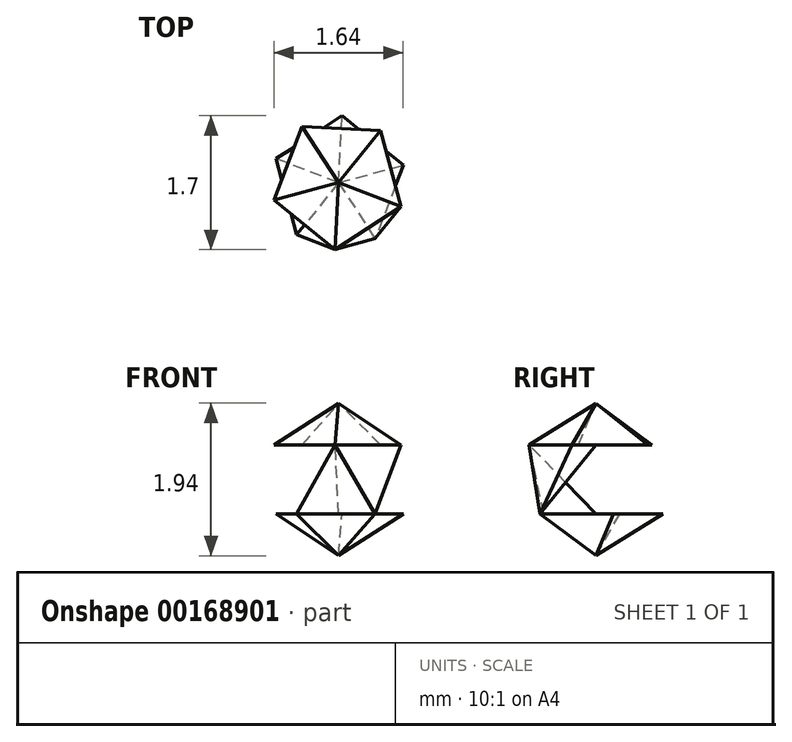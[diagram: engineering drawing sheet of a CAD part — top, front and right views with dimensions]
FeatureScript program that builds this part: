
annotation { "Feature Type Name" : "Feature", "Feature Type Description" : "" }
export const myFeature = defineFeature(function(context is Context, id is Id, definition is map)
    precondition{}
    {
        {
            var Q0;
            Q0=qCreatedBy(makeId("Top.planeOp"),FACE);
            var sketch = newSketch(context, id + "F0", { "sketchPlane" : qUnion([Q0])});
            skCircle(sketch, "E0.cCircle", {"center": v(0, 0) * mm, "radius": 0.69 * mm, "construction": true});
            skLineSegment(sketch, "E0.0", {"start": v(-0.04, -0.85) * mm, "end": v(-0.82, -0.22) * mm});
            skLineSegment(sketch, "E0.1", {"start": v(-0.82, -0.22) * mm, "end": v(-0.46, 0.71) * mm});
            skLineSegment(sketch, "E0.2", {"start": v(-0.46, 0.71) * mm, "end": v(0.53, 0.66) * mm});
            skLineSegment(sketch, "E0.3", {"start": v(0.53, 0.66) * mm, "end": v(0.8, -0.3) * mm});
            skLineSegment(sketch, "E0.4", {"start": v(0.8, -0.3) * mm, "end": v(-0.04, -0.85) * mm});
            skPoint(sketch, "E0.0.midPoint", {"position": v(-0.43, -0.54) * mm});
            skSolve(sketch);
        }
        {
            var Q0;
            Q0=qCreatedBy(makeId("Top.planeOp"),FACE);
            cPlane(context, id + "F1", {"entities" : qUnion([Q0]), "cplaneType" : CPlaneType.OFFSET, "offset" : 0.53 * mm, "width" : 150 * mm, "height" : 150 * mm});
        }
        {
            var Q0;
            Q0=qCreatedBy(id+"F1.planeOp",FACE);
            var sketch = newSketch(context, id + "F2", { "sketchPlane" : qUnion([Q0])});
            skPoint(sketch, "E1.0", {"position": v(0, 0) * mm});
            skSolve(sketch);
        }
        {
            var Q0;
            Q0=makeQuery(id+"F0.imprint","IMPRINT",FACE,{"disambiguationData":[TD([[makeQuery(id+"F0.imprint","IMPRINT",EDGE,{"derivedFrom":sQuery(id+"F0.wireOp",EDGE,"E0.0")}),-1.0]])]});
            var Q1;
            Q1=sQuery(id+"F2.wireOp",VERTEX,"E1.0");
            var Q2;
            Q2=sQuery(id+"F2.wireOp",VERTEX,"E1.0");
            var Q3;
            Q3=makeQuery(id+"F0.imprint","IMPRINT",FACE,{"disambiguationData":[TD([[makeQuery(id+"F0.imprint","IMPRINT",EDGE,{"derivedFrom":sQuery(id+"F0.wireOp",EDGE,"E0.0")}),-1.0]])]});
            loft(context, id + "F3", {"sheetProfilesArray" : [{ "sheetProfileEntities" : qUnion([Q0]) }, { "sheetProfileEntities" : qUnion([Q1]) }], "wireProfilesArray" : [{ "wireProfileEntities" : qUnion([Q2]) }, { "wireProfileEntities" : qUnion([Q3]) }]});
        }
        {
            var Q0;
            Q0=qCreatedBy(makeId("Top.planeOp"),FACE);
            var sketch = newSketch(context, id + "F4", { "sketchPlane" : qUnion([Q0])});
            skPoint(sketch, "E2.0", {"position": v(0.66, 0.18) * mm});
            skLineSegment(sketch, "E3", {"start": v(0, 0) * mm, "end": v(0.66, 0.18) * mm, "construction": true});
            skLineSegment(sketch, "E4", {"start": v(0.66, 0.18) * mm, "end": v(0.82, 0.22) * mm, "construction": true});
            skCircle(sketch, "E5.cCircle", {"center": v(0, 0) * mm, "radius": 0.69 * mm, "construction": true});
            skLineSegment(sketch, "E5.0", {"start": v(0.82, 0.22) * mm, "end": v(0.46, -0.71) * mm, "construction": true});
            skLineSegment(sketch, "E5.1", {"start": v(0.46, -0.71) * mm, "end": v(-0.53, -0.66) * mm, "construction": true});
            skLineSegment(sketch, "E5.2", {"start": v(-0.53, -0.66) * mm, "end": v(-0.8, 0.3) * mm, "construction": true});
            skLineSegment(sketch, "E5.3", {"start": v(-0.8, 0.3) * mm, "end": v(0.04, 0.85) * mm, "construction": true});
            skLineSegment(sketch, "E5.4", {"start": v(0.04, 0.85) * mm, "end": v(0.82, 0.22) * mm, "construction": true});
            skPoint(sketch, "E5.0.midPoint", {"position": v(0.64, -0.25) * mm});
            skSolve(sketch);
        }
        {
            var Q0;
            Q0=qCreatedBy(makeId("Top.planeOp"),FACE);
            cPlane(context, id + "F5", {"entities" : qUnion([Q0]), "cplaneType" : CPlaneType.OFFSET, "offset" : .88113 * mm, "oppositeDirection" : true, "width" : 150 * mm, "height" : 150 * mm});
        }
        {
            var Q0;
            Q0=qCreatedBy(id+"F5.planeOp",FACE);
            var sketch = newSketch(context, id + "F6", { "sketchPlane" : qUnion([Q0])});
            skLineSegment(sketch, "E6.0", {"start": v(0.46, -0.71) * mm, "end": v(-0.53, -0.66) * mm});
            skLineSegment(sketch, "E7.0", {"start": v(-0.53, -0.66) * mm, "end": v(-0.8, 0.3) * mm});
            skLineSegment(sketch, "E8.0", {"start": v(-0.8, 0.3) * mm, "end": v(0.04, 0.85) * mm});
            skLineSegment(sketch, "E9.0", {"start": v(0.04, 0.85) * mm, "end": v(0.82, 0.22) * mm});
            skLineSegment(sketch, "E10.0", {"start": v(0.82, 0.22) * mm, "end": v(0.46, -0.71) * mm});
            skSolve(sketch);
        }
        {
            var Q0;
            Q0=qCreatedBy(id+"F5.planeOp",FACE);
            cPlane(context, id + "F7", {"entities" : qUnion([Q0]), "cplaneType" : CPlaneType.OFFSET, "offset" : .52573 * mm, "oppositeDirection" : true, "width" : 150 * mm, "height" : 150 * mm});
        }
        {
            var Q0;
            Q0=qCreatedBy(id+"F7.planeOp",FACE);
            var sketch = newSketch(context, id + "F8", { "sketchPlane" : qUnion([Q0])});
            skPoint(sketch, "E11.0", {"position": v(0, 0) * mm});
            skSolve(sketch);
        }
        {
            var Q0;
            Q0=sQuery(id+"F8.wireOp",VERTEX,"E11.0");
            var Q1;
            Q1=makeQuery(id+"F6.imprint","IMPRINT",FACE,{"disambiguationData":[TD([[makeQuery(id+"F6.imprint","IMPRINT",EDGE,{"derivedFrom":sQuery(id+"F6.wireOp",EDGE,"E6.0")}),-1.0]])]});
            var Q2;
            Q2=makeQuery(id+"F6.imprint","IMPRINT",FACE,{"disambiguationData":[TD([[makeQuery(id+"F6.imprint","IMPRINT",EDGE,{"derivedFrom":sQuery(id+"F6.wireOp",EDGE,"E6.0")}),-1.0]])]});
            var Q3;
            Q3=sQuery(id+"F8.wireOp",VERTEX,"E11.0");
            loft(context, id + "F9", {"sheetProfilesArray" : [{ "sheetProfileEntities" : qUnion([Q0]) }, { "sheetProfileEntities" : qUnion([Q1]) }], "wireProfilesArray" : [{ "wireProfileEntities" : qUnion([Q2]) }, { "wireProfileEntities" : qUnion([Q3]) }]});
        }
        {
            var Q0;
            Q0=makeQuery(id+"F3.opLoft","CAP_FACE",FACE,{"disambiguationData":[OSD([makeQuery(id+"F0.imprint","IMPRINT",FACE,{"disambiguationData":[TD([[makeQuery(id+"F0.imprint","IMPRINT",EDGE,{"derivedFrom":sQuery(id+"F0.wireOp",EDGE,"E0.0")}),-1.0]])]})])],"isStart":true});
            var sketch = newSketch(context, id + "F10", { "sketchPlane" : qUnion([Q0])});
            skLineSegment(sketch, "E12", {"start": v(0, 0) * mm, "end": v(-0.04, 0.85) * mm});
            skLineSegment(sketch, "E13.1.0", {"start": v(0, 0) * mm, "end": v(-0.82, 0.22) * mm});
            skLineSegment(sketch, "E13.2.0", {"start": v(0, 0) * mm, "end": v(-0.46, -0.71) * mm});
            skLineSegment(sketch, "E13.3.0", {"start": v(0, 0) * mm, "end": v(0.53, -0.66) * mm});
            skLineSegment(sketch, "E13.4.0", {"start": v(0, 0) * mm, "end": v(0.8, 0.3) * mm});
            skPoint(sketch, "E13.center", {"position": v(0, 0) * mm});
            skSolve(sketch);
        }
        {
            var Q0;
            Q0=makeQuery(id+"F9.opLoft","CAP_FACE",FACE,{"disambiguationData":[OSD([makeQuery(id+"F6.imprint","IMPRINT",FACE,{"disambiguationData":[TD([[makeQuery(id+"F6.imprint","IMPRINT",EDGE,{"derivedFrom":sQuery(id+"F6.wireOp",EDGE,"E6.0")}),-1.0]])]})])],"isStart":true});
            var sketch = newSketch(context, id + "F11", { "sketchPlane" : qUnion([Q0])});
            skPoint(sketch, "E14.0", {"position": v(0, 0) * mm});
            skLineSegment(sketch, "E15", {"start": v(0, 0) * mm, "end": v(0.46, -0.71) * mm});
            skLineSegment(sketch, "E16.1.0", {"start": v(0, 0) * mm, "end": v(0.82, 0.22) * mm});
            skLineSegment(sketch, "E16.2.0", {"start": v(0, 0) * mm, "end": v(0.04, 0.85) * mm});
            skLineSegment(sketch, "E16.3.0", {"start": v(0, 0) * mm, "end": v(-0.8, 0.3) * mm});
            skLineSegment(sketch, "E16.4.0", {"start": v(0, 0) * mm, "end": v(-0.53, -0.66) * mm});
            skSolve(sketch);
        }
        {
            var Q1;
            Q1=makeQuery(id+"F11.imprint","IMPRINT",FACE,{"disambiguationData":[TD([[makeQuery(id+"F11.imprint","IMPRINT",EDGE,{"derivedFrom":sQuery(id+"F11.wireOp",EDGE,"E15")}),-1.0]])]});
            var Q2;
            Q2=sQuery(id+"F10.wireOp",VERTEX,"E12.end");
            loft(context, id + "F12", {"operationType" : NewBodyOperationType.ADD, "sheetProfilesArray" : [{ "sheetProfileEntities" : qUnion([Q1]) }, { "sheetProfileEntities" : qUnion([Q2]) }]});
        }
        {
            var Q1;
            Q1=makeQuery(id+"F10.imprint","IMPRINT",FACE,{"disambiguationData":[TD([[makeQuery(id+"F10.imprint","IMPRINT",EDGE,{"derivedFrom":sQuery(id+"F10.wireOp",EDGE,"E12")}),-1.0]])]});
            var Q2;
            Q2=sQuery(id+"F11.wireOp",VERTEX,"E15.end");
            loft(context, id + "F13", {"operationType" : NewBodyOperationType.ADD, "sheetProfilesArray" : [{ "sheetProfileEntities" : qUnion([Q1]) }, { "sheetProfileEntities" : qUnion([Q2]) }]});
        }
    });
